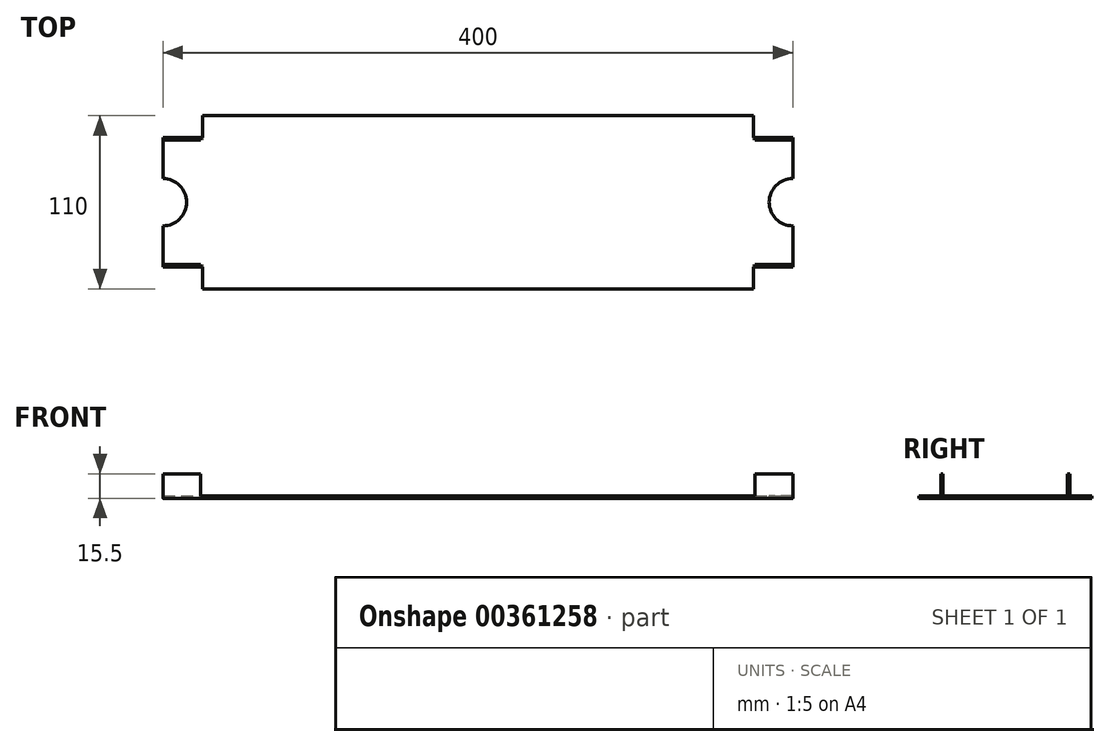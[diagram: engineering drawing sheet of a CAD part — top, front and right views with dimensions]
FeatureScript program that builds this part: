
annotation { "Feature Type Name" : "Feature", "Feature Type Description" : "" }
export const myFeature = defineFeature(function(context is Context, id is Id, definition is map)
    precondition{}
    {
        {
            var Q0;
            Q0=qCreatedBy(makeId("Top.planeOp"),FACE);
            var sketch = newSketch(context, id + "F0", { "sketchPlane" : qUnion([Q0])});
            skLineSegment(sketch, "E0.bottom", {"start": v(25, 14) * mm, "end": v(375, 14) * mm});
            skLineSegment(sketch, "E0.top", {"start": v(25, -96) * mm, "end": v(375, -96) * mm});
            skLineSegment(sketch, "E0.left", {"start": v(0, 0) * mm, "end": v(0, -26) * mm});
            skLineSegment(sketch, "E0.right", {"start": v(400, 0) * mm, "end": v(400, -26) * mm});
            skLineSegment(sketch, "E1", {"start": v(0, 0) * mm, "end": v(25, 0) * mm});
            skLineSegment(sketch, "E2", {"start": v(25, 0) * mm, "end": v(25, 14) * mm});
            skLineSegment(sketch, "E3", {"start": v(0, -82) * mm, "end": v(25, -82) * mm});
            skLineSegment(sketch, "E4", {"start": v(25, -82) * mm, "end": v(25, -96) * mm});
            skLineSegment(sketch, "E5", {"start": v(375, 14) * mm, "end": v(375, 0) * mm});
            skLineSegment(sketch, "E6", {"start": v(375, 0) * mm, "end": v(400, 0) * mm});
            skLineSegment(sketch, "E7", {"start": v(400, -82) * mm, "end": v(375, -82) * mm});
            skLineSegment(sketch, "E8", {"start": v(375, -82) * mm, "end": v(375, -96) * mm});
            skArc(sketch, "E9", {"start": v(0, -56) * mm, "mid": v(15, -41) * mm, "end": v(0, -26) * mm});
            skArc(sketch, "E10", {"start": v(400, -26) * mm, "mid": v(385, -41) * mm, "end": v(400, -56) * mm});
            skLineSegment(sketch, "E11.trimOffspring", {"start": v(0, -56) * mm, "end": v(0, -82) * mm});
            skLineSegment(sketch, "E12.trimOffspring", {"start": v(400, -56) * mm, "end": v(400, -82) * mm});
            skSolve(sketch);
        }
        {
            var Q0;
            Q0 = qSketchRegion(id + "F0", true);
            extrude(context, id + "F1", {"entities" : qUnion([Q0]), "depth" : 1.5 * mm});
        }
        {
            var Q0;
            Q0=makeQuery(id+"F1.opExtrude","CAP_FACE",FACE,{"disambiguationData":[OSD([sQuery(id+"F0.wireOp",EDGE,"E0.bottom"),sQuery(id+"F0.wireOp",EDGE,"E0.top"),sQuery(id+"F0.wireOp",EDGE,"E0.left"),sQuery(id+"F0.wireOp",EDGE,"E0.right"),sQuery(id+"F0.wireOp",EDGE,"E1"),sQuery(id+"F0.wireOp",EDGE,"E2"),sQuery(id+"F0.wireOp",EDGE,"E3"),sQuery(id+"F0.wireOp",EDGE,"E4"),sQuery(id+"F0.wireOp",EDGE,"E5"),sQuery(id+"F0.wireOp",EDGE,"E6"),sQuery(id+"F0.wireOp",EDGE,"E7"),sQuery(id+"F0.wireOp",EDGE,"E8")])],"isStart":false});
            var sketch = newSketch(context, id + "F2", { "sketchPlane" : qUnion([Q0])});
            skSolve(sketch);
        }
        {
            var Q0;
            Q0=makeQuery(id+"F2.imprint","IMPRINT",FACE,{"disambiguationData":[TD([[makeQuery(id+"F2.imprint","IMPRINT",EDGE,{"derivedFrom":makeQuery(id+"F1.opExtrude","CAP_EDGE",EDGE,{"disambiguationData":[OSD([sQuery(id+"F0.wireOp",EDGE,"E0.bottom")])],"isStart":false})}),-1.0]])]});
            var sketch = newSketch(context, id + "F3", { "sketchPlane" : qUnion([Q0])});
            skLineSegment(sketch, "E13.bottom", {"start": v(0, 0) * mm, "end": v(24, 0) * mm});
            skLineSegment(sketch, "E13.top", {"start": v(0, -1.5) * mm, "end": v(24, -1.5) * mm});
            skLineSegment(sketch, "E13.left", {"start": v(0, 0) * mm, "end": v(0, -1.5) * mm});
            skLineSegment(sketch, "E13.right", {"start": v(24, 0) * mm, "end": v(24, -1.5) * mm});
            skLineSegment(sketch, "E14.bottom", {"start": v(376, 0) * mm, "end": v(400, 0) * mm});
            skLineSegment(sketch, "E14.top", {"start": v(376, -1.5) * mm, "end": v(400, -1.5) * mm});
            skLineSegment(sketch, "E14.left", {"start": v(376, 0) * mm, "end": v(376, -1.5) * mm});
            skLineSegment(sketch, "E14.right", {"start": v(400, 0) * mm, "end": v(400, -1.5) * mm});
            skLineSegment(sketch, "E15", {"start": v(0, 0) * mm, "end": v(0, -82) * mm, "construction": true});
            skLineSegment(sketch, "E16", {"start": v(0, -41) * mm, "end": v(68.3, -41) * mm, "construction": true});
            skPoint(sketch, "E16.endSnap0", {"position": v(0, -41) * mm});
            skLineSegment(sketch, "E17.MirrorCS", {"start": v(0, -82) * mm, "end": v(0, -80.5) * mm});
            skLineSegment(sketch, "E18.MirrorCS", {"start": v(24, -82) * mm, "end": v(24, -80.5) * mm});
            skLineSegment(sketch, "E19.MirrorCS", {"start": v(400, -82) * mm, "end": v(400, -80.5) * mm});
            skLineSegment(sketch, "E20.MirrorCS", {"start": v(376, -82) * mm, "end": v(376, -80.5) * mm});
            skLineSegment(sketch, "E21.MirrorCS", {"start": v(0, -82) * mm, "end": v(24, -82) * mm});
            skLineSegment(sketch, "E22.MirrorCS", {"start": v(0, -80.5) * mm, "end": v(24, -80.5) * mm});
            skLineSegment(sketch, "E23.MirrorCS", {"start": v(376, -80.5) * mm, "end": v(400, -80.5) * mm});
            skLineSegment(sketch, "E24.MirrorCS", {"start": v(376, -82) * mm, "end": v(400, -82) * mm});
            skSolve(sketch);
        }
        {
            var Q0;
            Q0 = qSketchRegion(id + "F3", true);
            extrude(context, id + "F4", {"entities" : qUnion([Q0]), "operationType" : NewBodyOperationType.ADD, "depth" : 14 * mm});
        }
        {
            var Q0;
            Q0=makeQuery(id+"F1.opExtrude","CAP_EDGE",EDGE,{"disambiguationData":[OSD([sQuery(id+"F0.wireOp",EDGE,"E1")])],"isStart":true});
            var Q1;
            Q1=makeQuery(id+"F1.opExtrude","CAP_EDGE",EDGE,{"disambiguationData":[OSD([sQuery(id+"F0.wireOp",EDGE,"E3")])],"isStart":true});
            var Q2;
            Q2=makeQuery(id+"F1.opExtrude","CAP_EDGE",EDGE,{"disambiguationData":[OSD([sQuery(id+"F0.wireOp",EDGE,"E7")])],"isStart":true});
            var Q3;
            Q3=makeQuery(id+"F1.opExtrude","CAP_EDGE",EDGE,{"disambiguationData":[OSD([sQuery(id+"F0.wireOp",EDGE,"E6")])],"isStart":true});
            fillet(context, id + "F5", {"entities" : qUnion([Q0, Q1, Q2, Q3]), "radius" : 1.5 * mm, "tangentPropagation" : true, "allowEdgeOverflow" : false});
        }
    });
